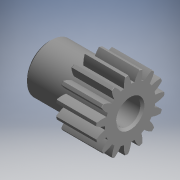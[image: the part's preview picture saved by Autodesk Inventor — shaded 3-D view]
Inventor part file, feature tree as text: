
AUTODESK INVENTOR PART (.ipt)
format: ipt  version: 2017.3 (Build 213256000, 256)  size: 251,904 bytes
history: native  units: mm (DEFAULTED — no unit token found)
features: sketch x2, revolve x1, extrude x1
ambient origin geometry x8: Origin, YZ Plane, XZ Plane, XY Plane, X Axis, Y Axis, Z Axis, Center Point
bodies: Solid1 (feature_tree)
feature tree (4):
  revolve  "Revolution1"  [1 undecoded]
  extrude  "Extrusion1"  [1 undecoded]
  sketch  "Sketch_8"  dims[d0=360.0deg d1=10.0mm d2=0.0mm]
  sketch  "Sketch_11"
note: 2 required parameter values undecoded (feature->parameter linkage not recoverable at this tier; creation-order binding heuristic only, values carry confidence <= 0.55)